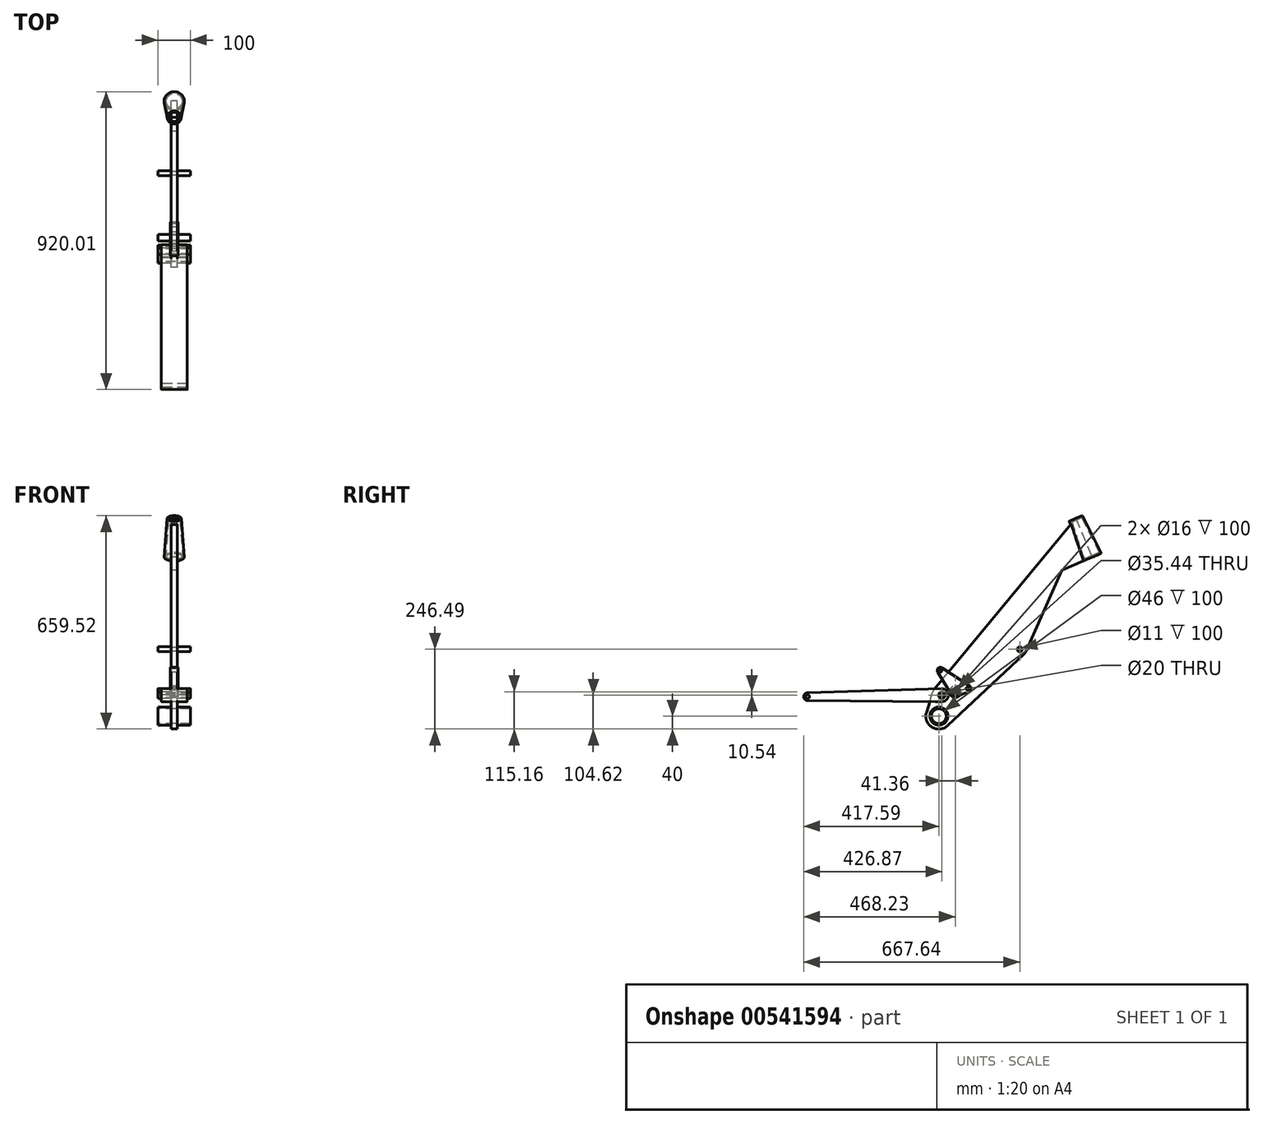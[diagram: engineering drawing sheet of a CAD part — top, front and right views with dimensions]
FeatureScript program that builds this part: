
annotation { "Feature Type Name" : "Feature", "Feature Type Description" : "" }
export const myFeature = defineFeature(function(context is Context, id is Id, definition is map)
    precondition{}
    {
        {
            var Q0;
            Q0=qCreatedBy(makeId("Right.planeOp"),FACE);
            var sketch = newSketch(context, id + "F0", { "sketchPlane" : qUnion([Q0])});
            skLineSegment(sketch, "E0", {"start": v(0, 0) * mm, "end": v(-93.36, 219.95) * mm, "construction": true});
            skLineSegment(sketch, "E1", {"start": v(-323.73, 632.13) * mm, "end": v(-11.64, -103.1) * mm, "construction": true});
            skPoint(sketch, "E2", {"position": v(-238.4, 431.12) * mm});
            skLineSegment(sketch, "E3", {"start": v(-303.73, 403.4) * mm, "end": v(-173.08, 458.85) * mm, "construction": true});
            skCircle(sketch, "E4", {"center": v(0, -8.13) * mm, "radius": 375.7 * mm, "construction": true});
            skPoint(sketch, "E5", {"position": v(-289.3, 551) * mm});
            skPoint(sketch, "E6", {"position": v(-712.3, -60) * mm});
            skPoint(sketch, "E7", {"position": v(-1117.88, 0) * mm});
            skLineSegment(sketch, "E8", {"start": v(-1117.88, 0) * mm, "end": v(0, 0) * mm, "construction": true});
            skCircle(sketch, "E9", {"center": v(-1117.88, 0) * mm, "radius": 375.7 * mm, "construction": true});
            skLineSegment(sketch, "E10", {"start": v(-712.3, -60) * mm, "end": v(-933.24, 662.68) * mm, "construction": true});
            skLineSegment(sketch, "E11", {"start": v(-289.3, 551) * mm, "end": v(-947.84, 551) * mm, "construction": true});
            skPoint(sketch, "E12", {"position": v(-899.1, 551) * mm});
            skLineSegment(sketch, "E13", {"start": v(-237.36, 573.04) * mm, "end": v(-341.22, 528.96) * mm, "construction": true});
            skPoint(sketch, "E14", {"position": v(-277.57, 523.38) * mm});
            skLineSegment(sketch, "E15", {"start": v(-712.3, -60) * mm, "end": v(-277.57, 523.38) * mm, "construction": true});
            skPoint(sketch, "E16", {"position": v(-814.62, 274.7) * mm});
            skLineSegment(sketch, "E17", {"start": v(-814.62, 274.7) * mm, "end": v(-277.57, 523.38) * mm, "construction": true});
            skPoint(sketch, "E18", {"position": v(-546.1, 399.05) * mm});
            skSolve(sketch);
        }
        {
            var Q0;
            Q0=qCreatedBy(makeId("Right.planeOp"),FACE);
            var sketch = newSketch(context, id + "F1", { "sketchPlane" : qUnion([Q0])});
            skLineSegment(sketch, "E19", {"start": v(-262.34, 420.96) * mm, "end": v(-264.3, 425.56) * mm});
            skLineSegment(sketch, "E20", {"start": v(-303.45, 539.56) * mm, "end": v(-264.3, 425.56) * mm});
            skLineSegment(sketch, "E21", {"start": v(-303.45, 539.56) * mm, "end": v(-305.4, 544.16) * mm});
            skLineSegment(sketch, "E22", {"start": v(-305.4, 544.16) * mm, "end": v(-309.35, 542.48) * mm});
            skLineSegment(sketch, "E23", {"start": v(-309.35, 542.48) * mm, "end": v(-266.94, 419) * mm});
            skLineSegment(sketch, "E24", {"start": v(-266.94, 419) * mm, "end": v(-262.34, 420.96) * mm});
            skSolve(sketch);
        }
        {
            var Q0;
            Q0=qSketchRegion(id+"F1",true);
            var Q1;
            Q1=sQuery(id+"F0.wireOp",EDGE,"E1");
            revolve(context, id + "F2", {"entities" : qUnion([Q0]), "axis" : qUnion([Q1]), "revolveType" : RevolveType.FULL});
        }
        {
            var Q0;
            Q0=qCreatedBy(makeId("Right.planeOp"),FACE);
            var sketch = newSketch(context, id + "F3", { "sketchPlane" : qUnion([Q0])});
            skCircle(sketch, "E25", {"center": v(-712.3, -60) * mm, "radius": 23 * mm});
            skCircle(sketch, "E26", {"center": v(-712.3, -60) * mm, "radius": 28 * mm});
            skSolve(sketch);
        }
        {
            var Q0;
            Q0=qSketchRegion(id+"F3",true);
            extrude(context, id + "F4", {"entities" : qUnion([Q0]), "operationType" : NewBodyOperationType.ADD, "endBound" : BoundingType.SYMMETRIC, "depth" : 100 * mm});
        }
        {
            var Q0;
            Q0=qCreatedBy(makeId("Right.planeOp"),FACE);
            var sketch = newSketch(context, id + "F5", { "sketchPlane" : qUnion([Q0])});
            skPoint(sketch, "E27", {"position": v(-703.01, 4.62) * mm});
            skPoint(sketch, "E28", {"position": v(-661.65, 15.16) * mm});
            skPoint(sketch, "E29", {"position": v(-462.24, 146.5) * mm});
            skSolve(sketch);
        }
        {
            var Q0;
            Q0=qCreatedBy(makeId("Right.planeOp"),FACE);
            var sketch = newSketch(context, id + "F6", { "sketchPlane" : qUnion([Q0])});
            skArc(sketch, "E30", {"start": v(-750.55, -48.32) * mm, "mid": v(-733.46, -93.94) * mm, "end": v(-684.97, -89.21) * mm});
            skLineSegment(sketch, "E31", {"start": v(-332.3, 391.27) * mm, "end": v(-238.4, 431.12) * mm});
            skLineSegment(sketch, "E32", {"start": v(-289.3, 551) * mm, "end": v(-238.4, 431.12) * mm});
            skCircle(sketch, "E33", {"center": v(-712.3, -60) * mm, "radius": 28 * mm});
            skArc(sketch, "E34", {"start": v(-726.11, 23.76) * mm, "mid": v(-729.42, 18.85) * mm, "end": v(-731.7, 13.38) * mm});
            skLineSegment(sketch, "E35.trimOffspring", {"start": v(-726.11, 23.76) * mm, "end": v(-289.3, 551) * mm});
            skCircle(sketch, "E36", {"center": v(-661.65, 15.16) * mm, "radius": 10 * mm});
            skCircle(sketch, "E37", {"center": v(-703.01, 4.62) * mm, "radius": 10 * mm});
            skCircle(sketch, "E38", {"center": v(-462.24, 146.5) * mm, "radius": 7.5 * mm});
            skCircle(sketch, "E39", {"center": v(-661.65, 15.16) * mm, "radius": 17.72 * mm});
            skArc(sketch, "E40", {"start": v(-448.58, 131.88) * mm, "mid": v(-445.93, 134.91) * mm, "end": v(-443.94, 138.41) * mm});
            skLineSegment(sketch, "E41", {"start": v(-332.3, 391.27) * mm, "end": v(-443.94, 138.41) * mm});
            skLineSegment(sketch, "E42", {"start": v(-684.97, -89.21) * mm, "end": v(-448.58, 131.88) * mm});
            skLineSegment(sketch, "E43", {"start": v(-750.55, -48.32) * mm, "end": v(-731.7, 13.38) * mm});
            skSolve(sketch);
        }
        {
            var Q0;
            Q0=qSketchRegion(id+"F6",true);
            extrude(context, id + "F7", {"entities" : qUnion([Q0]), "operationType" : NewBodyOperationType.ADD, "endBound" : BoundingType.SYMMETRIC, "depth" : 20 * mm});
        }
        {
            var Q0;
            Q0=qCreatedBy(makeId("Right.planeOp"),FACE);
            var sketch = newSketch(context, id + "F8", { "sketchPlane" : qUnion([Q0])});
            skCircle(sketch, "E44", {"center": v(-462.24, 146.5) * mm, "radius": 7.5 * mm});
            skCircle(sketch, "E45", {"center": v(-703.01, 4.62) * mm, "radius": 10 * mm});
            skCircle(sketch, "E46", {"center": v(-661.65, 15.16) * mm, "radius": 10 * mm});
            skCircle(sketch, "E47", {"center": v(-462.24, 146.5) * mm, "radius": 5.5 * mm});
            skCircle(sketch, "E48", {"center": v(-703.01, 4.62) * mm, "radius": 8 * mm});
            skCircle(sketch, "E49", {"center": v(-661.65, 15.16) * mm, "radius": 8 * mm});
            skSolve(sketch);
        }
        {
            var Q0;
            Q0=qSketchRegion(id+"F8",true);
            extrude(context, id + "F9", {"entities" : qUnion([Q0]), "operationType" : NewBodyOperationType.ADD, "endBound" : BoundingType.SYMMETRIC, "depth" : 100 * mm});
        }
        {
            var Q0;
            Q0=qCreatedBy(makeId("Right.planeOp"),FACE);
            var sketch = newSketch(context, id + "F10", { "sketchPlane" : qUnion([Q0])});
            skLineSegment(sketch, "E50", {"start": v(-1117.97, -12) * mm, "end": v(-703.17, -15.38) * mm});
            skArc(sketch, "E51", {"start": v(-703.17, -15.38) * mm, "mid": v(-683.01, 4.84) * mm, "end": v(-703.62, 24.61) * mm});
            skCircle(sketch, "E52", {"center": v(-1117.88, 0) * mm, "radius": 6 * mm});
            skCircle(sketch, "E53", {"center": v(-703.01, 4.62) * mm, "radius": 10 * mm});
            skArc(sketch, "E54", {"start": v(-1118.24, 12) * mm, "mid": v(-1129.88, -0.13) * mm, "end": v(-1117.97, -12) * mm});
            skLineSegment(sketch, "E55", {"start": v(-1118.24, 12) * mm, "end": v(-703.62, 24.61) * mm});
            skCircle(sketch, "E56", {"center": v(-722.27, -7.82) * mm, "radius": 7.5 * mm});
            skSolve(sketch);
        }
        {
            var Q0;
            Q0=qSketchRegion(id+"F10",true);
            extrude(context, id + "F11", {"entities" : qUnion([Q0]), "endBound" : BoundingType.SYMMETRIC, "depth" : 80 * mm, "offsetDistance" : 25 * mm});
        }
        {
            var Q0;
            Q0=qCreatedBy(makeId("Right.planeOp"),FACE);
            var sketch = newSketch(context, id + "F12", { "sketchPlane" : qUnion([Q0])});
            skPoint(sketch, "E57", {"position": v(-707.58, 80.75) * mm});
            skPoint(sketch, "E58", {"position": v(-623.02, 25.15) * mm});
            skArc(sketch, "E59", {"start": v(-702.09, 89.1) * mm, "mid": v(-714.53, 87.94) * mm, "end": v(-716.11, 75.54) * mm});
            skArc(sketch, "E60", {"start": v(-674.45, 7.34) * mm, "mid": v(-666.4, 0.93) * mm, "end": v(-656.1, 1.22) * mm});
            skArc(sketch, "E61", {"start": v(-619.32, 15.86) * mm, "mid": v(-613.07, 24.14) * mm, "end": v(-617.53, 33.5) * mm});
            skCircle(sketch, "E62", {"center": v(-707.58, 80.75) * mm, "radius": 5 * mm});
            skCircle(sketch, "E63", {"center": v(-623.02, 25.15) * mm, "radius": 5 * mm});
            skLineSegment(sketch, "E64", {"start": v(-656.1, 1.22) * mm, "end": v(-619.32, 15.86) * mm});
            skLineSegment(sketch, "E65", {"start": v(-617.53, 33.5) * mm, "end": v(-702.09, 89.1) * mm});
            skLineSegment(sketch, "E66", {"start": v(-716.11, 75.54) * mm, "end": v(-674.45, 7.34) * mm});
            skSolve(sketch);
        }
        {
            var Q0;
            Q0=qSketchRegion(id+"F12",true);
            extrude(context, id + "F13", {"entities" : qUnion([Q0]), "endBound" : BoundingType.SYMMETRIC, "depth" : 25 * mm});
        }
    });
